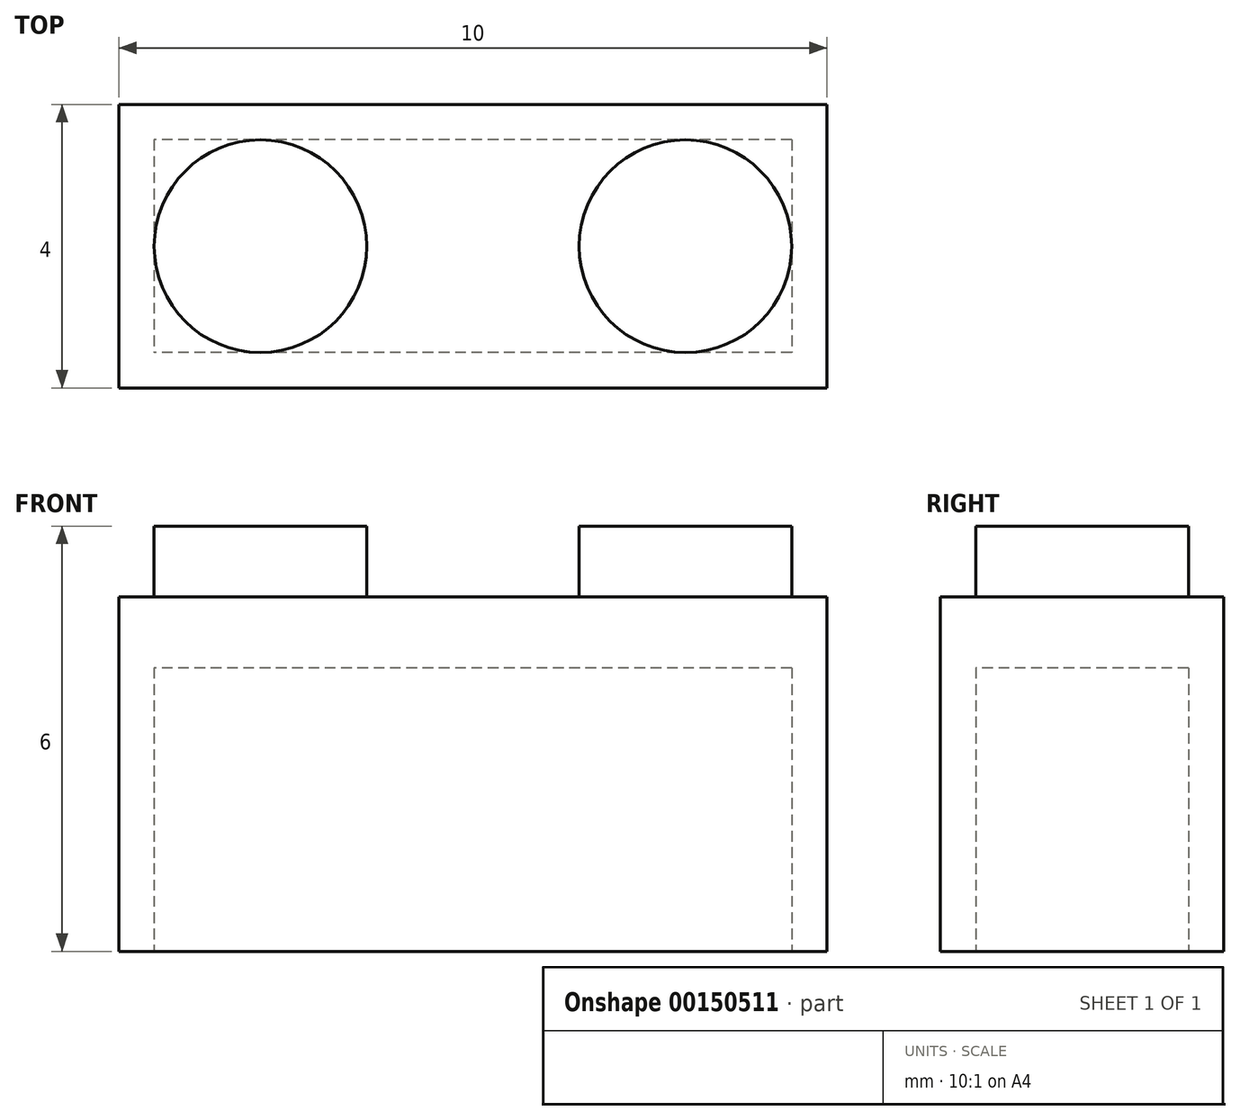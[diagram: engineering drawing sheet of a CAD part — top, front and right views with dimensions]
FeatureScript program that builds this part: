
annotation { "Feature Type Name" : "Feature", "Feature Type Description" : "" }
export const myFeature = defineFeature(function(context is Context, id is Id, definition is map)
    precondition{}
    {
        {
            var Q0;
            Q0=qCreatedBy(makeId("Top.planeOp"),FACE);
            var sketch = newSketch(context, id + "F0", { "sketchPlane" : qUnion([Q0])});
            skLineSegment(sketch, "E0.bottom", {"start": v(5, -2) * mm, "end": v(-5, -2) * mm});
            skLineSegment(sketch, "E0.top", {"start": v(5, 2) * mm, "end": v(-5, 2) * mm});
            skLineSegment(sketch, "E0.left", {"start": v(5, -2) * mm, "end": v(5, 2) * mm});
            skLineSegment(sketch, "E0.right", {"start": v(-5, -2) * mm, "end": v(-5, 2) * mm});
            skPoint(sketch, "E0.middle", {"position": v(0, 0) * mm});
            skSolve(sketch);
        }
        {
            var Q0;
            Q0 = qSketchRegion(id + "F0", true);
            extrude(context, id + "F1", {"entities" : qUnion([Q0]), "depth" : 5 * mm});
        }
        {
            var Q0;
            Q0=makeQuery(id+"F1.opExtrude","CAP_FACE",FACE,{"disambiguationData":[OSD([sQuery(id+"F0.wireOp",EDGE,"E0.bottom"),sQuery(id+"F0.wireOp",EDGE,"E0.top"),sQuery(id+"F0.wireOp",EDGE,"E0.left"),sQuery(id+"F0.wireOp",EDGE,"E0.right")])],"isStart":false});
            var sketch = newSketch(context, id + "F2", { "sketchPlane" : qUnion([Q0])});
            skCircle(sketch, "E1", {"center": v(-3, 0) * mm, "radius": 1.5 * mm});
            skCircle(sketch, "E2", {"center": v(3, 0) * mm, "radius": 1.5 * mm});
            skSolve(sketch);
        }
        {
            var Q0;
            Q0=makeQuery(id+"F2.imprint","IMPRINT",FACE,{"disambiguationData":[TD([[makeQuery(id+"F2.imprint","IMPRINT",EDGE,{"derivedFrom":sQuery(id+"F2.wireOp",EDGE,"E1")}),1.0]])]});
            var Q1;
            Q1=makeQuery(id+"F2.imprint","IMPRINT",FACE,{"disambiguationData":[TD([[makeQuery(id+"F2.imprint","IMPRINT",EDGE,{"derivedFrom":sQuery(id+"F2.wireOp",EDGE,"E2")}),1.0]])]});
            extrude(context, id + "F3", {"entities" : qUnion([Q0, Q1]), "operationType" : NewBodyOperationType.ADD, "depth" : 1 * mm});
        }
        {
            var Q0;
            Q0=qCreatedBy(makeId("Top.planeOp"),FACE);
            var sketch = newSketch(context, id + "F4", { "sketchPlane" : qUnion([Q0])});
            skLineSegment(sketch, "E3.bottom", {"start": v(4.5, 1.5) * mm, "end": v(-4.5, 1.5) * mm});
            skLineSegment(sketch, "E3.top", {"start": v(4.5, -1.5) * mm, "end": v(-4.5, -1.5) * mm});
            skLineSegment(sketch, "E3.left", {"start": v(4.5, 1.5) * mm, "end": v(4.5, -1.5) * mm});
            skLineSegment(sketch, "E3.right", {"start": v(-4.5, 1.5) * mm, "end": v(-4.5, -1.5) * mm});
            skPoint(sketch, "E3.middle", {"position": v(0, 0) * mm});
            skSolve(sketch);
        }
        {
            var Q0;
            Q0 = qSketchRegion(id + "F4", true);
            extrude(context, id + "F5", {"entities" : qUnion([Q0]), "operationType" : NewBodyOperationType.REMOVE, "depth" : 4 * mm});
        }
    });
